# Revit family: Bateria_czasowa_umywalkowa_stojaca_9002
name_source: partatom
category: Plumbing Fixtures
units: mm (PartAtom-declared; Revit-internal decimal feet)

## family parameters
Cut with Voids When Loaded = No
Host = Face
Part Type = Normal
Room Calculation Point = No
Round Connector Dimension = Use Diameter
Shared = No

## types (1)
- Bateria_czasowa_umywalkowa_stojaca_9002
    Default Elevation = 1219 mm
    Depth / Glebokosc = 103 mm  [stored 0.337927 ft]
    Description = Cechy:
- Wysoka odporność na akty wandalizmu dzięki wykonaniu z najwyższej jakości materiałów
- Prosta obsługa
- Łatwy montaż
    Height / Wysokosc = 104 mm
    Manufacturer = faneco.com
    Manufacturer code / Kod producenta = 5901764296881
    Material = Mosiadz chromowany
    Material finish / Wykonczenie = Mosiądz pokryty chromem
    Product code / Kod produktu = FAN9002
    Type Comments = Bateria czasowa umywalkowa stojąca 9002
    URL = https://faneco.com
    Weight / Waga = 0.46 kg
    Width / Szerokosc = 42 mm  [stored 0.137795 ft]

note: [stored X ft] marks values corroborated as IEEE doubles in the binary element streams (Revit-internal decimal feet)

## geometry (parser evidence)
native form markers: Sweep x4
no freeform markers — native parametric forms only
